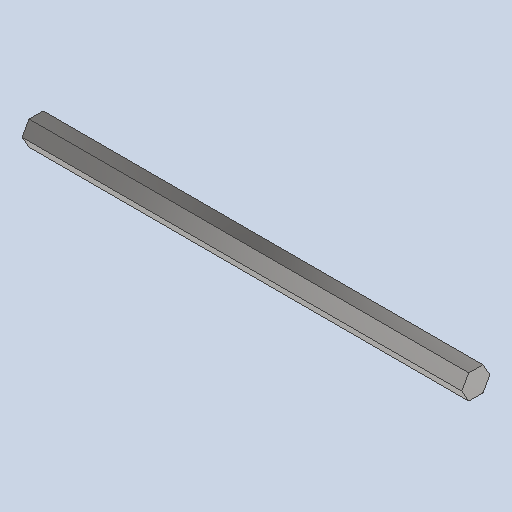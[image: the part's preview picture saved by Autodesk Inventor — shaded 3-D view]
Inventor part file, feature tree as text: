
AUTODESK INVENTOR PART (.ipt)
format: ipt  version: 2023 (Build 270158000, 158)  size: 95,744 bytes
history: native  units: in
note: dims shown in document units (in); Inventor stores cm internally (conversion verified against a paired STEP export)
features: extrude x1, sketch x1
ambient origin geometry x8: Origin, YZ Plane, XZ Plane, XY Plane, X Axis, Y Axis, Z Axis, Center Point
bodies: Solid1 (feature_tree)
feature tree (2):
  extrude  "Extrusion1"  Depth=9.0in TaperAngle=0.0deg
  sketch  "Sketch1"  dims[d0=0.5in d1=9.0in d2=0.0in]
